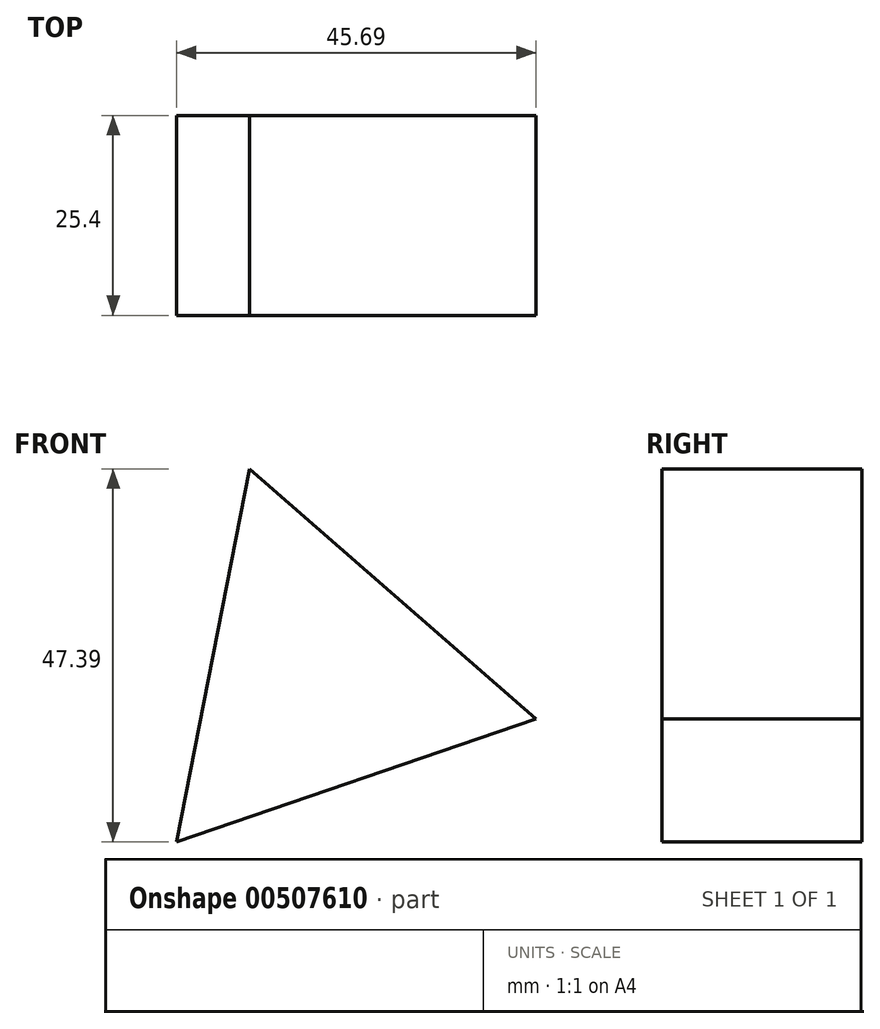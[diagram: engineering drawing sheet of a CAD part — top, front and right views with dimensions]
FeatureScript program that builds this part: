
annotation { "Feature Type Name" : "Feature", "Feature Type Description" : "" }
export const myFeature = defineFeature(function(context is Context, id is Id, definition is map)
    precondition{}
    {
        {
            var Q0;
            Q0=qCreatedBy(makeId("Front.planeOp"),FACE);
            var sketch = newSketch(context, id + "F0", { "sketchPlane" : qUnion([Q0])});
            skCircle(sketch, "E0.cCircle", {"center": v(0, 0) * mm, "radius": 27.88 * mm, "construction": true});
            skLineSegment(sketch, "E0.0", {"start": v(-9.04, 26.38) * mm, "end": v(27.36, -5.36) * mm});
            skLineSegment(sketch, "E0.1", {"start": v(27.36, -5.36) * mm, "end": v(-18.33, -21.01) * mm});
            skLineSegment(sketch, "E0.2", {"start": v(-18.33, -21.01) * mm, "end": v(-9.04, 26.38) * mm});
            skSolve(sketch);
        }
        {
            var Q0;
            Q0=makeQuery(id+"F0.imprint","IMPRINT",FACE,{"disambiguationData":[TD([[makeQuery(id+"F0.imprint","IMPRINT",EDGE,{"derivedFrom":sQuery(id+"F0.wireOp",EDGE,"E0.0")}),-1.0]])]});
            extrude(context, id + "F1", {"entities" : qUnion([Q0]), "depth" : 25.4 * mm});
        }
    });
